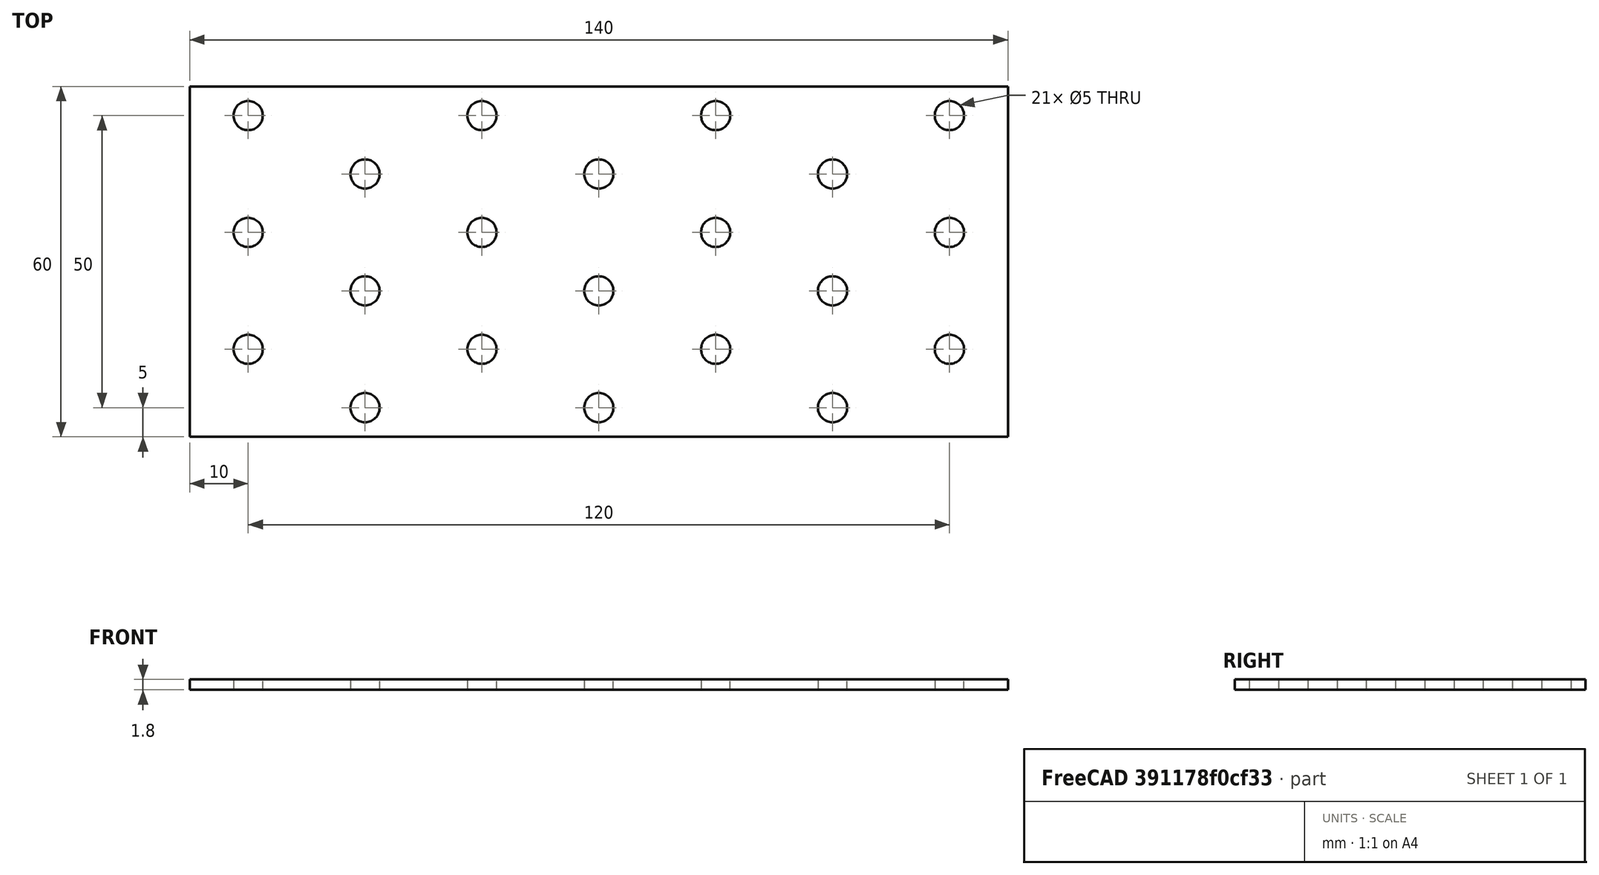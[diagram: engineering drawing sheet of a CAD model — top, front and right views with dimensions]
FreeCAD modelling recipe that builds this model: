
FCSTD DOCUMENT  (FreeCAD 0.19R24276 (Git))
Label: Bar_60x140__1_8mm
License: All rights reserved
LicenseURL: http://en.wikipedia.org/wiki/All_rights_reserved
objects: Sketcher::SketchObject×1, PartDesign::Pad×1, PartDesign::Body×1
note: 4 computed .brp shape members not serialized (recipe doc carries the construction recipe); baked Part::Feature solids carry a one-line shape summary decoded from their .brp

FEATURE [Sketcher::SketchObject] Sketch
  FullyConstrained = false
  MapMode = 5
  Support = -> [XY_Plane]
  sketch-geometry (47):
    g0: LineSegment StartX=0 StartY=0 StartZ=0 EndX=120 EndY=0 EndZ=0
    g1: LineSegment StartX=120 StartY=0 StartZ=0 EndX=120 EndY=80 EndZ=0
    g2: LineSegment StartX=120 StartY=80 StartZ=0 EndX=0 EndY=80 EndZ=0
    g3: LineSegment StartX=0 StartY=80 StartZ=0 EndX=0 EndY=0 EndZ=0
    g4: LineSegment StartX=0 StartY=4.5 StartZ=0 EndX=120 EndY=4.5 EndZ=0
    g5: LineSegment StartX=0 StartY=24.5 StartZ=0 EndX=120 EndY=24.5 EndZ=0
    g6: LineSegment StartX=0 StartY=44.5 StartZ=0 EndX=120 EndY=44.5 EndZ=0
    g7: LineSegment StartX=0 StartY=64.5 StartZ=0 EndX=120 EndY=64.5 EndZ=0
    g8: LineSegment StartX=48.5 StartY=0 StartZ=0 EndX=48.5 EndY=4.5 EndZ=0
    g9: LineSegment StartX=68.5 StartY=0 StartZ=0 EndX=68.5 EndY=4.5 EndZ=0
    g10: LineSegment StartX=88.5 StartY=0 StartZ=0 EndX=88.5 EndY=4.5 EndZ=0
    g11: LineSegment StartX=108.5 StartY=0 StartZ=0 EndX=108.5 EndY=4.5 EndZ=0
    g12: LineSegment StartX=0 StartY=14.5 StartZ=0 EndX=120 EndY=14.5 EndZ=0
    g13: LineSegment StartX=0 StartY=34.5 StartZ=0 EndX=120 EndY=34.5 EndZ=0
    g14: LineSegment StartX=0 StartY=54.5 StartZ=0 EndX=120 EndY=54.5 EndZ=0
    g15: LineSegment StartX=0 StartY=74.5 StartZ=0 EndX=120 EndY=74.5 EndZ=0
    g16: LineSegment StartX=48.5 StartY=24.5 StartZ=0 EndX=48.5 EndY=80 EndZ=0
    g17: LineSegment StartX=68.5 StartY=14.5 StartZ=0 EndX=68.5 EndY=80 EndZ=0
    g18: LineSegment StartX=88.5 StartY=24.5 StartZ=0 EndX=88.5 EndY=80 EndZ=0
    g19: LineSegment StartX=108.5 StartY=14.5 StartZ=0 EndX=108.5 EndY=80 EndZ=0
    g20: Circle CenterX=28.5 CenterY=14.5 CenterZ=0 NormalX=0 NormalY=0 NormalZ=1 AngleXU=0 Radius=2.5
    g21: Circle CenterX=108.5 CenterY=14.5 CenterZ=0 NormalX=0 NormalY=0 NormalZ=1 AngleXU=0 Radius=2.5
    g22: Circle CenterX=8.5 CenterY=24.5 CenterZ=0 NormalX=0 NormalY=0 NormalZ=1 AngleXU=0 Radius=2.5
    g23: Circle CenterX=48.5 CenterY=24.5 CenterZ=0 NormalX=0 NormalY=0 NormalZ=1 AngleXU=0 Radius=2.5
    g24: Circle CenterX=88.5 CenterY=24.5 CenterZ=0 NormalX=0 NormalY=0 NormalZ=1 AngleXU=0 Radius=2.5
    g25: Circle CenterX=8.5 CenterY=44.5 CenterZ=0 NormalX=0 NormalY=0 NormalZ=1 AngleXU=0 Radius=2.5
    g26: Circle CenterX=48.5 CenterY=44.5 CenterZ=0 NormalX=0 NormalY=0 NormalZ=1 AngleXU=0 Radius=2.5
    g27: Circle CenterX=88.5 CenterY=44.5 CenterZ=0 NormalX=0 NormalY=0 NormalZ=1 AngleXU=0 Radius=2.5
    g28: Circle CenterX=28.5 CenterY=54.5 CenterZ=0 NormalX=0 NormalY=0 NormalZ=1 AngleXU=0 Radius=2.5
    g29: Circle CenterX=68.5 CenterY=54.5 CenterZ=0 NormalX=0 NormalY=0 NormalZ=1 AngleXU=0 Radius=2.5
    g30: Circle CenterX=108.5 CenterY=54.5 CenterZ=0 NormalX=0 NormalY=0 NormalZ=1 AngleXU=0 Radius=2.5
    g31: Circle CenterX=88.5 CenterY=64.5 CenterZ=0 NormalX=0 NormalY=0 NormalZ=1 AngleXU=0 Radius=2.5
    g32: Circle CenterX=48.5 CenterY=64.5 CenterZ=0 NormalX=0 NormalY=0 NormalZ=1 AngleXU=0 Radius=2.5
    g33: Circle CenterX=8.5 CenterY=64.5 CenterZ=0 NormalX=0 NormalY=0 NormalZ=1 AngleXU=0 Radius=2.5
    g34: Circle CenterX=28.5 CenterY=34.5 CenterZ=0 NormalX=0 NormalY=0 NormalZ=1 AngleXU=0 Radius=2.5
    g35: Circle CenterX=68.5 CenterY=34.5 CenterZ=0 NormalX=0 NormalY=0 NormalZ=1 AngleXU=0 Radius=2.5
    g36: Circle CenterX=108.5 CenterY=34.5 CenterZ=0 NormalX=0 NormalY=0 NormalZ=1 AngleXU=0 Radius=2.5
    g37: LineSegment StartX=28.5 StartY=74.5 StartZ=0 EndX=28.5 EndY=14.5 EndZ=0
    g38: LineSegment StartX=8.5 StartY=4.5 StartZ=0 EndX=8.5 EndY=24.5 EndZ=0
    g39: Circle CenterX=68.5 CenterY=14.5 CenterZ=0 NormalX=0 NormalY=0 NormalZ=1 AngleXU=0 Radius=2.5
    g40: LineSegment StartX=-1.5 StartY=9.5 StartZ=0 EndX=138.5 EndY=9.5 EndZ=0
    g41: LineSegment StartX=-1.5 StartY=69.5 StartZ=0 EndX=138.5 EndY=69.5 EndZ=0
    g42: LineSegment StartX=-1.5 StartY=69.5 StartZ=0 EndX=-1.5 EndY=9.5 EndZ=0
    g43: LineSegment StartX=138.5 StartY=69.5 StartZ=0 EndX=138.5 EndY=9.5 EndZ=0
    g44: Circle CenterX=128.5 CenterY=24.5 CenterZ=0 NormalX=0 NormalY=0 NormalZ=1 AngleXU=0 Radius=2.5
    g45: Circle CenterX=128.5 CenterY=44.5 CenterZ=0 NormalX=0 NormalY=0 NormalZ=1 AngleXU=0 Radius=2.5
    g46: Circle CenterX=128.5 CenterY=64.5 CenterZ=0 NormalX=0 NormalY=0 NormalZ=1 AngleXU=0 Radius=2.5
  constraints (100):
    c: Coincident(g0,g1)
    c: Coincident(g1,g2)
    c: Coincident(g2,g3)
    c: Coincident(g3,g0)
    c: Horizontal(g0)
    c: Horizontal(g2)
    c: Vertical(g1)
    c: Vertical(g3)
    c: Coincident(g0,g-1)
    c: DistanceX(g0,g0) = 120
    c: DistanceY(g3,g3) = 80
    c: Horizontal(g4)
    c: PointOnObject(g4,g3)
    c: PointOnObject(g4,g1)
    c: Horizontal(g5)
    c: PointOnObject(g5,g3)
    c: PointOnObject(g5,g1)
    c: DistanceY(g4,g5) = 20
    c: Horizontal(g6)
    c: PointOnObject(g6,g1)
    c: PointOnObject(g6,g3)
    c: DistanceY(g5,g6) = 20
    c: Horizontal(g7)
    c: PointOnObject(g7,g1)
    c: PointOnObject(g7,g3)
    c: DistanceY(g6,g7) = 20
    c: Vertical(g8)
    c: Vertical(g9)
    c: Vertical(g10)
    c: Vertical(g11)
    c: PointOnObject(g8,g0)
    c: PointOnObject(g9,g0)
    c: PointOnObject(g10,g0)
    c: PointOnObject(g11,g0)
    c: PointOnObject(g19,g2)
    c: PointOnObject(g18,g2)
    c: PointOnObject(g17,g2)
    c: PointOnObject(g16,g2)
    c: DistanceX(g8,g9) = 20
    c: DistanceX(g9,g10) = 20
    c: DistanceX(g10,g11) = 20
    c: Horizontal(g12)
    c: Horizontal(g13)
    c: Horizontal(g14)
    c: Horizontal(g15)
    c: PointOnObject(g12,g3)
    c: PointOnObject(g13,g3)
    c: PointOnObject(g14,g3)
    c: PointOnObject(g15,g3)
    c: PointOnObject(g15,g1)
    c: PointOnObject(g14,g1)
    c: PointOnObject(g13,g1)
    c: PointOnObject(g12,g1)
    c: DistanceY(g0,g12) = 14.5
    c: DistanceY(g12,g13) = 20
    c: DistanceY(g13,g14) = 20
    c: DistanceY(g14,g15) = 20
    c: PointOnObject(g20,g12)
    c: PointOnObject(g8,g4)
    c: Tangent(g8,g16)
    c: PointOnObject(g9,g4)
    c: PointOnObject(g17,g12)
    c: Tangent(g9,g17)
    c: PointOnObject(g10,g4)
    c: Tangent(g10,g18)
    c: PointOnObject(g11,g4)
    c: PointOnObject(g19,g12)
    c: Tangent(g11,g19)
    c: Coincident(g21,g19)
    c: Diameter(g20) = 5
    c: PointOnObject(g16,g5)
    c: PointOnObject(g18,g5)
    c: Equal(g23,g24)
    c: Equal(g33,g28)
    c: Equal(g28,g32)
    c: Equal(g32,g31)
    c: Equal(g31,g30)
    c: Diameter(g28) = 5
    c: Equal(g31,g29)
    c: Equal(g26,g27)
    c: Diameter(g34) = 5
    c: Coincident(g37,g20)
    c: Vertical(g37)
    c: DistanceY(g0,g4) = 4.5
    c: Coincident(g38,g22)
    c: Vertical(g38)
    c: Coincident(g39,g17)
    c: Equal(g21,g39)
    c: Horizontal(g40)
    c: Horizontal(g41)
    c: Vertical(g42)
    c: DistanceX(g0,g38) = 8.5
    c: Coincident(g42,g40)
    c: Coincident(g41,g42)
    c: Vertical(g43)
    c: DistanceX(g40,g38) = 10
    c: Coincident(g40,g43)
    c: DistanceY(g40,g21) = 5
    c: Coincident(g41,g43)
    c: DistanceY(g40,g41) = 60
FEATURE [PartDesign::Pad] Pad
  Direction = (1,1,1)
  Length = 1.8
  Length2 = 100
  Profile = -> Sketch
  Type = 0
FEATURE [PartDesign::Body] Body
  Group = -> [Sketch,Pad]
  Origin = -> Origin
  Tip = -> Pad
